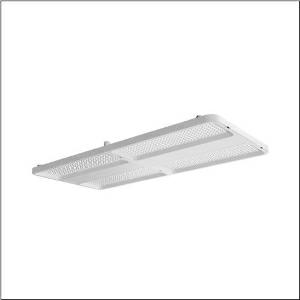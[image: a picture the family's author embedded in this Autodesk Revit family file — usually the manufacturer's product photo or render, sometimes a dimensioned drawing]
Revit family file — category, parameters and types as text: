
# Revit family: highbay_11_maxi_51hn11db4qda02
name_source: partatom
category: Lighting Fixtures
units: mm (PartAtom-declared; Revit-internal decimal feet)

## family parameters
Cut with Voids When Loaded = No
Host = Face
Light Source = No
Part Type = Normal
Room Calculation Point = No
Round Connector Dimension = Use Diameter
Shared = No

## types (1)
- --- (1 x LED, 36000 lm, 178.2 W, 4000K)
    Apparent Load = 178 VA
    CIE Flux Codes = 85 97 100 100 100
    Color Rendering = 80
    Color Temperature = 4000K
    Default Elevation = 1800 mm
    Description = high bay luminaire Highbay 11 maxi; direct symmetric narrow distribution, light control with lens of PMMA; UGR ≤ 22 (X = 4H | Y = 8H | S = 0.25H | reflection values 70/50/20); luminous flux: 36.000lm; light colour: 840, colour temperature: 4000K, MacAdam ≤ 2 SDCM (initial), colour rendering: CRI > 80; luminous efficacy: 202lm/W; rated service life: 100.000h (L95/B50) at AT= 25°C; control: Bluetooth® Mesh; for wireless networking: Node luminaire for setting up a local control solution without a higher-level application controller, intelligence completely in the luminaire; no control line such as DALI between the Node multi-sensor luminaires and Nodes is required, wireless integration of other Node luminaires and Node multi-sensor luminaires into the network is possible; number of Node luminaires in the project can be expanded as required, network sizes > 300 Nodes can be realized; can also be connected to lighting or building automation via various gateways upon request; integrated DALI2 ECG provides luminaire data (according to IEC62386, Part 251), energy data (Part 252), and monitoring and analytics data (Part 253) to higher-level systems for further processing; luminaire connection: terminal, 5-pole, max. 2.5mm² (cable entry for one cable, Ø 8.5..16mm); mains connection: 230..240V, AC 50/60Hz; connected load: 178,2W; protection rating (complete): IP66; insulation class (complete): insulation class I (protective earthing); protection symbol: D; impact resistance: IK08; certification: CE, ENEC, VDE, UKCA; internal wiring halogen-free; luminaire corresponds to IFS (International Featured Standards) requirements for safety and quality in the food industry; LABS conformity tested according to VDMA 24364:2018-05; housing frame of high-performance plastic PA6, matt traffic white (RAL 9016); cover of PMMA; dimension (LxWxH): 946 x 442 x 72mm; permissible operating ambient temperature: -20..+40°C (reducing of maximum allowable ambient temperature of 5°C with ceiling mounting); packaging unit: 1 piece; (delivery without accessories; please order mounting accessories separately)
    Height = 72 mm  [stored 0.23622 ft]
    Lamp = 1 x LED
    Lamp Light Flux = 36000 lm
    Lamp Power = 178.2 W
    Lamp count = 1
    Length = 946 mm
    Luminous efficacy = 202 lm/W
    Manufacturer = Siteco
    ModVariant = No
    Model = 51HN11DB4QDA02
    Mounting Place = Ceiling
    Mounting Type = Pendant
    Number of Poles = 1
    OnlyDefault = Yes
    Power Factor = 1
    Product Name = Highbay 11 maxi
    Product group = high bay luminaire
    ProductGroupID = 901
    Protection Class = Protection class I
    Protection Degree = IP 66
    RLX_Detail_Level = 1
    RLX_Emergency_Light_Flux = 0 lm
    RLX_Emergency_Type = 0
    RLX_Emergency_Type_DB = No
    RlxData = <blob elided: 127849 chars, md5=1353db21>
    Socket = socket
    Standby Power = 0 W
    System Light Flux = 36000 lm
    System Power = 178 W
    Type Comments = factory setting: luminous flux: 100 % | dim-lin: 254 | 824 mA
    Type Image = l_1363244.jpg
    URL = http://relux.com
    VarID = @adj_022587
    Voltage = 0 V
    Weight = 0.00 kg
    Width = 442 mm

note: [stored X ft] marks values corroborated as IEEE doubles in the binary element streams (Revit-internal decimal feet)

## geometry (parser evidence)
native form markers: Blend x4, Sweep x10
no freeform markers — native parametric forms only
